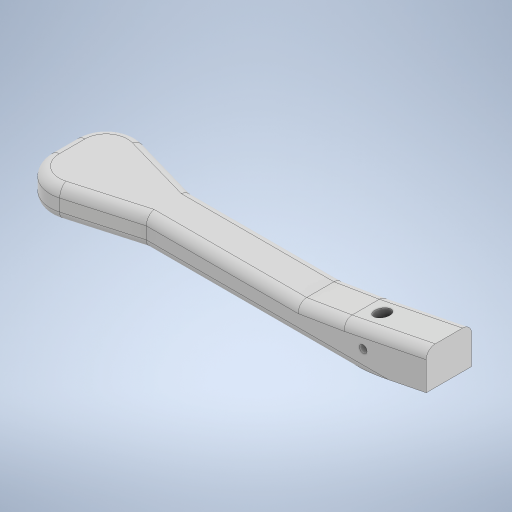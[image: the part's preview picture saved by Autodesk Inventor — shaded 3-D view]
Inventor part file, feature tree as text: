
AUTODESK INVENTOR PART (.ipt)
format: ipt  version: 2023 (Build 270158000, 158)  size: 348,160 bytes
history: native  units: mm
features: sketch x8, extrude x4, other x3, fillet x2, hole x1
ambient origin geometry x8: Origin, YZ Plane, XZ Plane, XY Plane, X Axis, Y Axis, Z Axis, Center Point
bodies: Body1 (feature_tree)
feature tree (18):
  other  "Твердое тело1"
  extrude  "Выдавливание1"  Depth=200.0mm
  fillet  "Сопряжение1"  Radius=30.0mm
  other  "РабПлоскость1"
  extrude  "Выдавливание2"  Depth=20.0mm
  sketch  "Эскиз4"
  other  "РабПлоскость2"
  sketch  "Эскиз5"
  extrude  "Выдавливание5"  Depth=20.0mm
  hole  "Отверстие1"  [1 undecoded]
  fillet  "Сопряжение5"  Radius=20.0mm
  extrude  "Выдавливание6"  Depth=20.0mm
  sketch  "Эскиз8"
  sketch  "Эскиз9"
  sketch  "Эскиз1"
  sketch  "Эскиз2"
  sketch  "Эскиз6"
  sketch  "Эскиз7"
note: 1 required parameter value undecoded (feature->parameter linkage not recoverable at this tier; creation-order binding heuristic only, values carry confidence <= 0.55)
